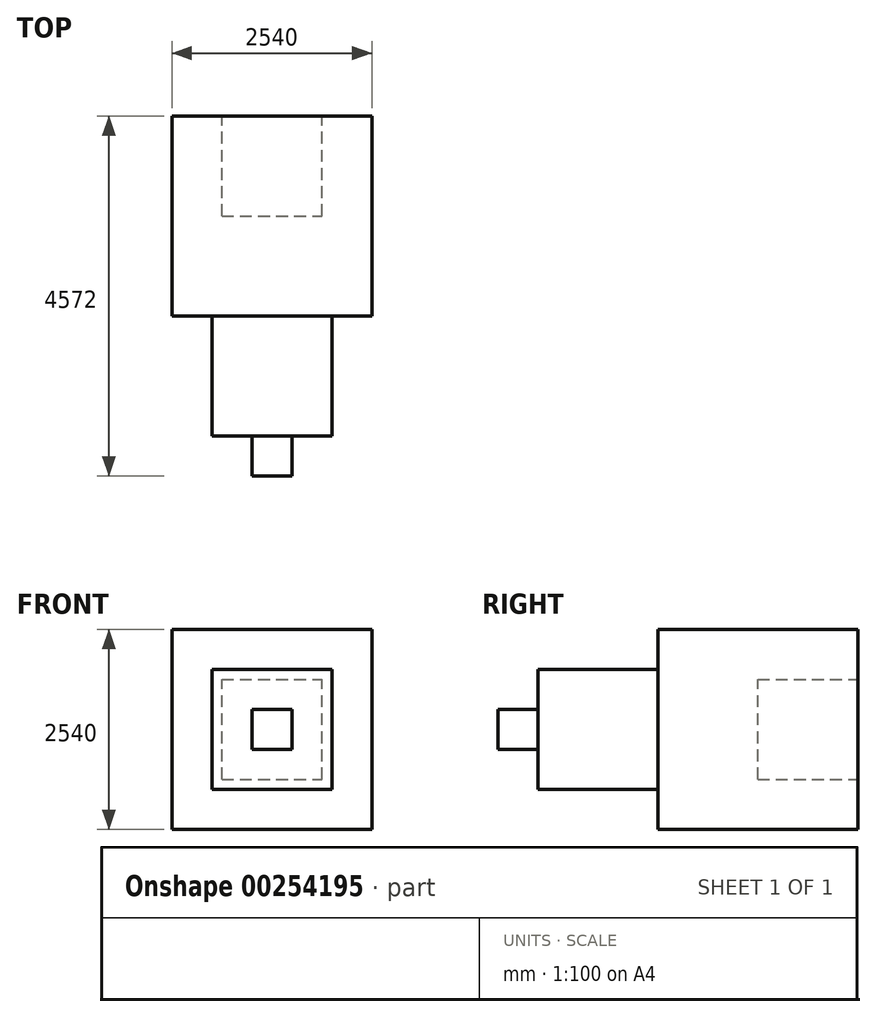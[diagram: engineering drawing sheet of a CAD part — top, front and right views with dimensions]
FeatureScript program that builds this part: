
annotation { "Feature Type Name" : "Feature", "Feature Type Description" : "" }
export const myFeature = defineFeature(function(context is Context, id is Id, definition is map)
    precondition{}
    {
        {
            var Q0;
            Q0=qCreatedBy(makeId("Right.planeOp"),FACE);
            var sketch = newSketch(context, id + "F0", { "sketchPlane" : qUnion([Q0])});
            skLineSegment(sketch, "E0.bottom", {"start": v(-1270, 1270) * mm, "end": v(1270, 1270) * mm});
            skLineSegment(sketch, "E0.top", {"start": v(-1270, -1270) * mm, "end": v(1270, -1270) * mm});
            skLineSegment(sketch, "E0.left", {"start": v(-1270, 1270) * mm, "end": v(-1270, -1270) * mm});
            skLineSegment(sketch, "E0.right", {"start": v(1270, 1270) * mm, "end": v(1270, -1270) * mm});
            skSolve(sketch);
        }
        {
            var Q0;
            Q0=makeQuery(id+"F0.imprint","IMPRINT",FACE,{"disambiguationData":[TD([[makeQuery(id+"F0.imprint","IMPRINT",EDGE,{"derivedFrom":sQuery(id+"F0.wireOp",EDGE,"E0.bottom")}),-1.0]])]});
            extrude(context, id + "F1", {"entities" : qUnion([Q0]), "depth" : 2540 * mm});
        }
        {
            var Q0;
            Q0=makeQuery(id+"F1.opExtrude","SWEPT_FACE",FACE,{"disambiguationData":[OSD([sQuery(id+"F0.wireOp",EDGE,"E0.left")])]});
            var sketch = newSketch(context, id + "F2", { "sketchPlane" : qUnion([Q0])});
            skLineSegment(sketch, "E1.bottom", {"start": v(508, -762) * mm, "end": v(2032, -762) * mm});
            skLineSegment(sketch, "E1.top", {"start": v(508, 762) * mm, "end": v(2032, 762) * mm});
            skLineSegment(sketch, "E1.left", {"start": v(508, -762) * mm, "end": v(508, 762) * mm});
            skLineSegment(sketch, "E1.right", {"start": v(2032, -762) * mm, "end": v(2032, 762) * mm});
            skSolve(sketch);
        }
        {
            var Q0;
            Q0=makeQuery(id+"F2.imprint","IMPRINT",FACE,{"disambiguationData":[TD([[makeQuery(id+"F2.imprint","IMPRINT",EDGE,{"derivedFrom":sQuery(id+"F2.wireOp",EDGE,"E1.bottom")}),1.0]])]});
            extrude(context, id + "F3", {"entities" : qUnion([Q0]), "operationType" : NewBodyOperationType.ADD, "depth" : 1524 * mm});
        }
        {
            var Q0;
            Q0=makeQuery(id+"F3.opExtrude","CAP_FACE",FACE,{"disambiguationData":[OSD([sQuery(id+"F2.wireOp",EDGE,"E1.bottom"),sQuery(id+"F2.wireOp",EDGE,"E1.top"),sQuery(id+"F2.wireOp",EDGE,"E1.left"),sQuery(id+"F2.wireOp",EDGE,"E1.right")])],"isStart":false});
            var sketch = newSketch(context, id + "F4", { "sketchPlane" : qUnion([Q0])});
            skLineSegment(sketch, "E2.bottom", {"start": v(1524, 254) * mm, "end": v(1016, 254) * mm});
            skLineSegment(sketch, "E2.top", {"start": v(1524, -254) * mm, "end": v(1016, -254) * mm});
            skLineSegment(sketch, "E2.left", {"start": v(1524, 254) * mm, "end": v(1524, -254) * mm});
            skLineSegment(sketch, "E2.right", {"start": v(1016, 254) * mm, "end": v(1016, -254) * mm});
            skSolve(sketch);
        }
        {
            var Q0;
            Q0=makeQuery(id+"F4.imprint","IMPRINT",FACE,{"disambiguationData":[TD([[makeQuery(id+"F4.imprint","IMPRINT",EDGE,{"derivedFrom":sQuery(id+"F4.wireOp",EDGE,"E2.bottom")}),1.0]])]});
            extrude(context, id + "F5", {"entities" : qUnion([Q0]), "operationType" : NewBodyOperationType.ADD, "depth" : 508 * mm});
        }
        {
            var Q0;
            Q0=makeQuery(id+"F1.opExtrude","SWEPT_FACE",FACE,{"disambiguationData":[OSD([sQuery(id+"F0.wireOp",EDGE,"E0.right")])]});
            var sketch = newSketch(context, id + "F6", { "sketchPlane" : qUnion([Q0])});
            skLineSegment(sketch, "E3.bottom", {"start": v(-635, -635) * mm, "end": v(-1905, -635) * mm});
            skLineSegment(sketch, "E3.top", {"start": v(-635, 635) * mm, "end": v(-1905, 635) * mm});
            skLineSegment(sketch, "E3.left", {"start": v(-635, -635) * mm, "end": v(-635, 635) * mm});
            skLineSegment(sketch, "E3.right", {"start": v(-1905, -635) * mm, "end": v(-1905, 635) * mm});
            skSolve(sketch);
        }
        {
            var Q0;
            Q0=makeQuery(id+"F6.imprint","IMPRINT",FACE,{"disambiguationData":[TD([[makeQuery(id+"F6.imprint","IMPRINT",EDGE,{"derivedFrom":sQuery(id+"F6.wireOp",EDGE,"E3.bottom")}),-1.0]])]});
            extrude(context, id + "F7", {"entities" : qUnion([Q0]), "operationType" : NewBodyOperationType.REMOVE, "oppositeDirection" : true, "depth" : 1270 * mm});
        }
    });
